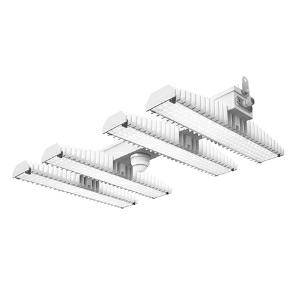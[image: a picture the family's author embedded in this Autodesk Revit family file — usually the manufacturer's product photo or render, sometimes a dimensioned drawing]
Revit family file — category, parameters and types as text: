
# Revit family: 3f_filippi_-_3f_lem_sensor_ampio_3f_filippi_-_59255_a0812_-_3f_lem_4_led_200_dali_sensor_cr_ampio___vs_e81f
name_source: partatom
category: Lighting Fixtures
units: mm (PartAtom-declared; Revit-internal decimal feet)

## family parameters
Cut with Voids When Loaded = No
Host = Face
Light Source = No
Part Type = Normal
Room Calculation Point = No
Round Connector Dimension = Use Diameter
Shared = No

## types (1)
- 3F Filippi - 3F LEM Sensor Ampio (1 x LED, 26607 lm, 219 W, 4000 K)
    Apparent Load = 219 VA
    Approval mark = ENEC
    CIE Flux Codes = 67 90 97 100 100
    Color Rendering = 80
    Color Temperature = 4000 K
    Control Gear = Electronic transformer
    Default Elevation = 1800 mm
    Description = Industrial luminaire with high light output and high luminous efficiency designed with the most innovative technologies for environments with temperature up to 50°C.

ILLUMINOTECHNICAL
Luminous efficiency 100% (DLOR 98%, ULOR 2%).
Initial luminous flux of the luminaire 26607 lm.
Direct symmetric wide distribution: the illuminated area has a rectangular shape.
Installation Interdistance Transv.D = 1.24 x hu - Long.D = 1.20 x hu.
Tabular UGR (CIE 117 - 4H-8H; S=0.25H; 70/50/20): RUG 22.8 - 22.9.
Beam angle: 82° - 83°.
Luminous efficacy 121 lm/W.
Lifetime (L93/B10): 30000 h. (tq+25°C)
Lifetime (L90/B10): 50000 h. (tq+25°C)
Lifetime (L85/B10): 80000 h. (tq+25°C)
Lifetime (L80/B10): 100000 h. (tq+25°C)
Lifetime (L85/B10): 50000 h. (tq+50°C)
Sudden decreased luminous flux after 50000 hours: 0% (C0).
Photobiological safety in compliance with IEC/TR 62778: RG0 risk exempt, (IEC 62471).
In compliance with IEC/EN 62722-2-1 - IEC/EN 62717 standards.

SOURCE
4 Mid-Power linear LED modules 50W/840.
Energy efficiency class (UE 2019/2020 - UE 2019/2015): C.
CIE 13.3 Colour rendering index: CRI >80 (R9 <50%).
IES TM-30 Fidelity Index: Rf = 84 Rg = 95.
CCT nominal colour temperature 4000 K.
Colour initial tolerance (MacAdam): SDCM 3.

MECHANICAL
Passive modular heatsinks in die-casted aluminium, painted in white colour.
To optimize the thermal management of the LED module, the heatsinks are oversized and provided with self-cleaning of cooling fins.
Wiring body in aluminium and galvanised steel anchored solidly to the sinks and thermally separated.
3F Lens lenses with high luminous efficiency, transparent methacrylate (PMMA), fixed to the LED modules.
Fixing brackets in stainless steel.
Luminaire with limited surface temperature. - D - (EN 60598-2-24)
Dimensions: 952x542 mm, height 133 mm. Weight 19.94 kg.
IP54 protection degree.
Mechanical strength to impacts IK04 (0.5 joule).
Glow-wire test resistance 650°C.

ELECTRICAL
Halogen Free DALI electronic wiring 230V-50/60Hz, power factor 0.90 at full load, THD <25%, constant output current, class I, 2 driver, 2 DALI addresses.
DALI light and presence sensor integrated in the luminarie.
Power of the luminaire 219 W.
CE - IEC 60598-1 - EN 60598-1.
Flicker: <4%.
Ambient temperature from -25°C to +50°C.
Temperature class T6 max 85°C.
Quick connection via M25 5P connector with 9-13 mm tightening range.
Power unit positioned on a separate compartment by the LED module to ensure optimum temperatures of cabling components, to be inspectable and maintainable.
Relative humidity UR: <85%.

INSTALLATION
Ceiling / Suspended / Wall.
All accessories dedicated to this product are available on the Catalog and on our website www.3F-Filippi.com.

ACCESSORIES
A0812 - Anti-glare microprismatic VS moulded glass, tempered, not flammable, with sealing gasket.
One required for each light module. The pack contains 10 pieces.

APPLICATIONS
In commercial environments, exhibition and industrial areas, stores, open areas.
Applications with high ambient temperature up to 50°C.
Environments in which it is necessary a total protection against falling fragments (eg environments with foodstuffs or machines with moving parts or with extreme temperature changes), use luminaires with polycarbonate lenses.

LIGHT MANAGEMENT
The DALI presence and brightness sensor, integrated in the luminaire, allows you to keep the level of illumination constant as a function of natural light (in addition to switching on/off as a result of presence detection and set twilight threshold).
Recommended installation height up to 10 m.
Commissioning of the control system via free APP; the intervention of a specialist technician can be quoted on request.

WARNING
The luminaire cannot be controlled manually with PUSH-DIM technology.
Fixture not suitable for cold stores with an ambient temperature <0°C and/or relative humidity >85%.
Luminaire designed for disposal/recycling at end-of-life.
Replaceable (LED only) light source by a professional. Replaceable control gear by a professional.
    Height = 133 mm  [stored 0.436352 ft]
    Lamp = 1 x LED
    Lamp Light Flux = 26607 lm
    Lamp Power = 219 W
    Lamp count = 1
    Length = 952 mm
    Lifetime = 50000 h
    Luminous efficacy = 121 lm/W
    Manufacturer = 3F Filippi
    ModVariant = No
    Model = 3F Filippi - 59255+A0812 - 3F LEM 4 LED 200 DALI Sensor CR AMPIO + VS
    Mounting Place = Ceiling
    Mounting Type = Pendant
    Number of Poles = 1
    OnlyDefault = Yes
    Power Factor = 1
    Product Name = 3F Filippi - 3F LEM Sensor Ampio
    Product group = pendant luminaire
    ProductGroupID = 9
    Protection Class = Protection class I
    Protection Degree = IP 54
    RLX_Detail_Level = 1
    RLX_Emergency_Light_Flux = 0 lm
    RLX_Emergency_Type = 0
    RLX_Emergency_Type_DB = No
    RlxData = <blob elided: 123169 chars, md5=434b4cdb>
    Socket = socket
    Standby Power = 0 W
    System Light Flux = 26606 lm
    System Power = 219 W
    Type Comments = Product without accessories
    Type Image = 3f_filippi_-_lem_4_sensor__a0812.jpg
    URL = http://relux.com
    VarID = ---
    Voltage = 0 V
    Weight = 0.00 kg
    Width = 542 mm

note: [stored X ft] marks values corroborated as IEEE doubles in the binary element streams (Revit-internal decimal feet)

## geometry (parser evidence)
native form markers: Blend x4, Sweep x11
no freeform markers — native parametric forms only
